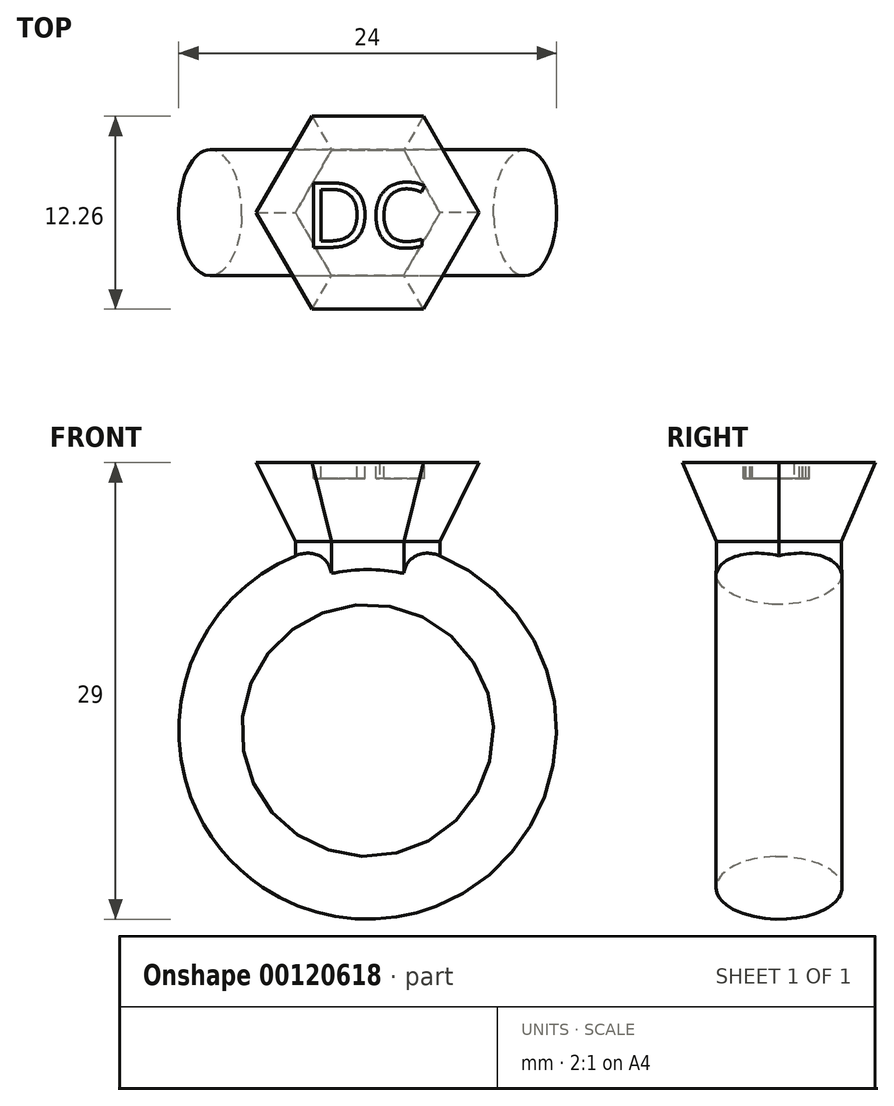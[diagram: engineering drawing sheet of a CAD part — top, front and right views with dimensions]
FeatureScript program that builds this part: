
annotation { "Feature Type Name" : "Feature", "Feature Type Description" : "" }
export const myFeature = defineFeature(function(context is Context, id is Id, definition is map)
    precondition{}
    {
        {
            var Q0;
            Q0=qCreatedBy(makeId("Top.planeOp"),FACE);
            var sketch = newSketch(context, id + "F0", { "sketchPlane" : qUnion([Q0])});
            skLineSegment(sketch, "E0", {"start": v(0, 25.8) * mm, "end": v(0, -37.93) * mm, "construction": true});
            skSolve(sketch);
        }
        {
            var Q0;
            Q0=qCreatedBy(makeId("Top.planeOp"),FACE);
            var sketch = newSketch(context, id + "F1", { "sketchPlane" : qUnion([Q0])});
            skEllipse(sketch, "E1", {"center": v(10, 0) * mm, "majorRadius": 4 * mm, "minorRadius": 2 * mm, "majorAxis": v(0, 1)});
            skSolve(sketch);
        }
        {
            var Q0;
            Q0=makeQuery(id+"F1.imprint","IMPRINT",FACE,{"disambiguationData":[TD([[makeQuery(id+"F1.imprint","IMPRINT",EDGE,{"derivedFrom":sQuery(id+"F1.wireOp",EDGE,"E1")}),1.0]])]});
            var Q1;
            Q1=sQuery(id+"F0.wireOp",EDGE,"E0");
            revolve(context, id + "F2", {"entities" : qUnion([Q0]), "axis" : qUnion([Q1]), "revolveType" : RevolveType.FULL});
        }
        {
            var Q0;
            Q0=qCreatedBy(makeId("Top.planeOp"),FACE);
            cPlane(context, id + "F3", {"entities" : qUnion([Q0]), "cplaneType" : CPlaneType.OFFSET, "offset" : 12 * mm, "width" : 150 * mm, "height" : 150 * mm});
        }
        {
            var Q0;
            Q0=qCreatedBy(id+"F3.planeOp",FACE);
            var sketch = newSketch(context, id + "F4", { "sketchPlane" : qUnion([Q0])});
            skCircle(sketch, "E2.cCircle", {"center": v(0, 0) * mm, "radius": 3.98 * mm, "construction": true});
            skLineSegment(sketch, "E2.0", {"start": v(-2.3, 3.98) * mm, "end": v(2.3, 3.98) * mm});
            skLineSegment(sketch, "E2.1", {"start": v(2.3, 3.98) * mm, "end": v(4.6, 0) * mm});
            skLineSegment(sketch, "E2.2", {"start": v(4.6, 0) * mm, "end": v(2.3, -3.98) * mm});
            skLineSegment(sketch, "E2.3", {"start": v(2.3, -3.98) * mm, "end": v(-2.3, -3.98) * mm});
            skLineSegment(sketch, "E2.4", {"start": v(-2.3, -3.98) * mm, "end": v(-4.6, 0) * mm});
            skLineSegment(sketch, "E2.5", {"start": v(-4.6, 0) * mm, "end": v(-2.3, 3.98) * mm});
            skPoint(sketch, "E2.0.midPoint", {"position": v(0, 3.98) * mm});
            skSolve(sketch);
        }
        {
            var Q0;
            Q0=makeQuery(id+"F4.imprint","IMPRINT",FACE,{"disambiguationData":[TD([[makeQuery(id+"F4.imprint","IMPRINT",EDGE,{"derivedFrom":sQuery(id+"F4.wireOp",EDGE,"E2.0")}),-1.0]])]});
            extrude(context, id + "F5", {"entities" : qUnion([Q0]), "operationType" : NewBodyOperationType.ADD, "oppositeDirection" : true, "depth" : 2 * mm});
        }
        {
            var Q0;
            Q0=makeQuery(id+"F5.opExtrude","CAP_FACE",FACE,{"disambiguationData":[OSD([sQuery(id+"F4.wireOp",EDGE,"E2.0"),sQuery(id+"F4.wireOp",EDGE,"E2.1"),sQuery(id+"F4.wireOp",EDGE,"E2.2"),sQuery(id+"F4.wireOp",EDGE,"E2.3"),sQuery(id+"F4.wireOp",EDGE,"E2.4"),sQuery(id+"F4.wireOp",EDGE,"E2.5")])],"isStart":true});
            cPlane(context, id + "F6", {"entities" : qUnion([Q0]), "cplaneType" : CPlaneType.OFFSET, "offset" : 5 * mm, "width" : 150 * mm, "height" : 150 * mm});
        }
        {
            var Q0;
            Q0=qCreatedBy(id+"F6.planeOp",FACE);
            var sketch = newSketch(context, id + "F7", { "sketchPlane" : qUnion([Q0])});
            skCircle(sketch, "E3.cCircle", {"center": v(0, 0) * mm, "radius": 6.13 * mm, "construction": true});
            skLineSegment(sketch, "E3.0", {"start": v(-3.54, 6.13) * mm, "end": v(3.54, 6.13) * mm});
            skLineSegment(sketch, "E3.1", {"start": v(3.54, 6.13) * mm, "end": v(7.08, 0) * mm});
            skLineSegment(sketch, "E3.2", {"start": v(7.08, 0) * mm, "end": v(3.54, -6.13) * mm});
            skLineSegment(sketch, "E3.3", {"start": v(3.54, -6.13) * mm, "end": v(-3.54, -6.13) * mm});
            skLineSegment(sketch, "E3.4", {"start": v(-3.54, -6.13) * mm, "end": v(-7.08, 0) * mm});
            skLineSegment(sketch, "E3.5", {"start": v(-7.08, 0) * mm, "end": v(-3.54, 6.13) * mm});
            skPoint(sketch, "E3.0.midPoint", {"position": v(0, 6.13) * mm});
            skSolve(sketch);
        }
        {
            var Q1;
            Q1=makeQuery(id+"F7.imprint","IMPRINT",FACE,{"disambiguationData":[TD([[makeQuery(id+"F7.imprint","IMPRINT",EDGE,{"derivedFrom":sQuery(id+"F7.wireOp",EDGE,"E3.0")}),-1.0]])]});
            var Q2;
            Q2=makeQuery(id+"F5.opExtrude","CAP_FACE",FACE,{"disambiguationData":[OSD([sQuery(id+"F4.wireOp",EDGE,"E2.0"),sQuery(id+"F4.wireOp",EDGE,"E2.1"),sQuery(id+"F4.wireOp",EDGE,"E2.2"),sQuery(id+"F4.wireOp",EDGE,"E2.3"),sQuery(id+"F4.wireOp",EDGE,"E2.4"),sQuery(id+"F4.wireOp",EDGE,"E2.5")])],"isStart":true});
            loft(context, id + "F8", {"operationType" : NewBodyOperationType.ADD, "sheetProfilesArray" : [{ "sheetProfileEntities" : qUnion([Q1]) }, { "sheetProfileEntities" : qUnion([Q2]) }]});
        }
        {
            var Q0;
            Q0=makeQuery(id+"F8.opLoft","CAP_FACE",FACE,{"disambiguationData":[OSD([makeQuery(id+"F7.imprint","IMPRINT",FACE,{"disambiguationData":[TD([[makeQuery(id+"F7.imprint","IMPRINT",EDGE,{"derivedFrom":sQuery(id+"F7.wireOp",EDGE,"E3.0")}),-1.0]])]})])],"isStart":true});
            var sketch = newSketch(context, id + "F9", { "sketchPlane" : qUnion([Q0])});
            skPoint(sketch, "E4.secondSnap0", {"position": v(5.3, -3.06) * mm});
            skText(sketch, "E5", { "text": "DC", "fontName": "OpenSans-Regular.ttf"});
            const initialGuessF9  = {"E5": [-0.00399, -0.0022, 1, 0, 0.00412]};
            skSetInitialGuess(sketch, initialGuessF9);
            skSolve(sketch);
        }
        {
            var Q0;
            Q0 = qSketchRegion(id + "F9", true);
            extrude(context, id + "F10", {"entities" : qUnion([Q0]), "operationType" : NewBodyOperationType.REMOVE, "oppositeDirection" : true, "depth" : 1 * mm});
        }
    });
